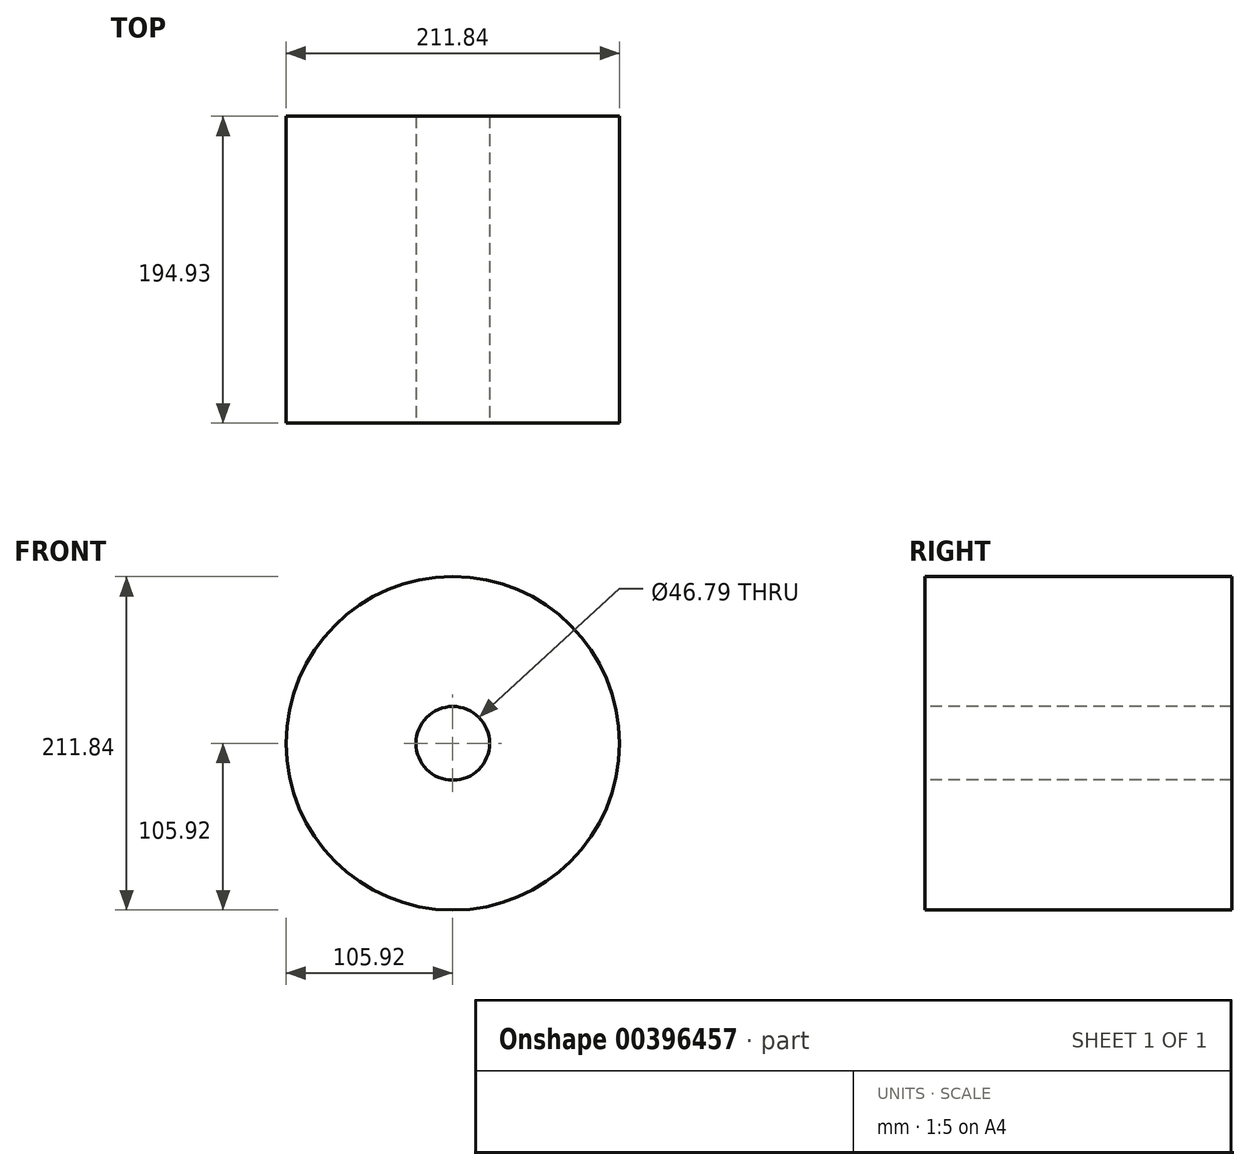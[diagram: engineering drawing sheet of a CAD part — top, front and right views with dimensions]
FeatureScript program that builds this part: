
annotation { "Feature Type Name" : "Feature", "Feature Type Description" : "" }
export const myFeature = defineFeature(function(context is Context, id is Id, definition is map)
    precondition{}
    {
        {
            var Q0;
            Q0=qCreatedBy(makeId("Right.planeOp"),FACE);
            var sketch = newSketch(context, id + "F0", { "sketchPlane" : qUnion([Q0])});
            skLineSegment(sketch, "E0.bottom", {"start": v(-159.37, 76.57) * mm, "end": v(35.56, 76.57) * mm});
            skLineSegment(sketch, "E0.top", {"start": v(-159.37, -5.96) * mm, "end": v(35.56, -5.96) * mm});
            skLineSegment(sketch, "E0.left", {"start": v(-159.37, 76.57) * mm, "end": v(-159.37, -5.96) * mm});
            skLineSegment(sketch, "E0.right", {"start": v(35.56, 76.57) * mm, "end": v(35.56, -5.96) * mm});
            skSolve(sketch);
        }
        {
            var Q0;
            Q0=qCreatedBy(makeId("Right.planeOp"),FACE);
            var sketch = newSketch(context, id + "F1", { "sketchPlane" : qUnion([Q0])});
            skLineSegment(sketch, "E1", {"start": v(-170.77, -29.35) * mm, "end": v(82.77, -29.35) * mm});
            skSolve(sketch);
        }
        {
            var Q0;
            Q0 = qSketchRegion(id + "F0", true);
            var Q1;
            Q1=sQuery(id+"F1.wireOp",EDGE,"E1");
            revolve(context, id + "F2", {"entities" : qUnion([Q0]), "axis" : qUnion([Q1]), "revolveType" : RevolveType.FULL});
        }
    });
